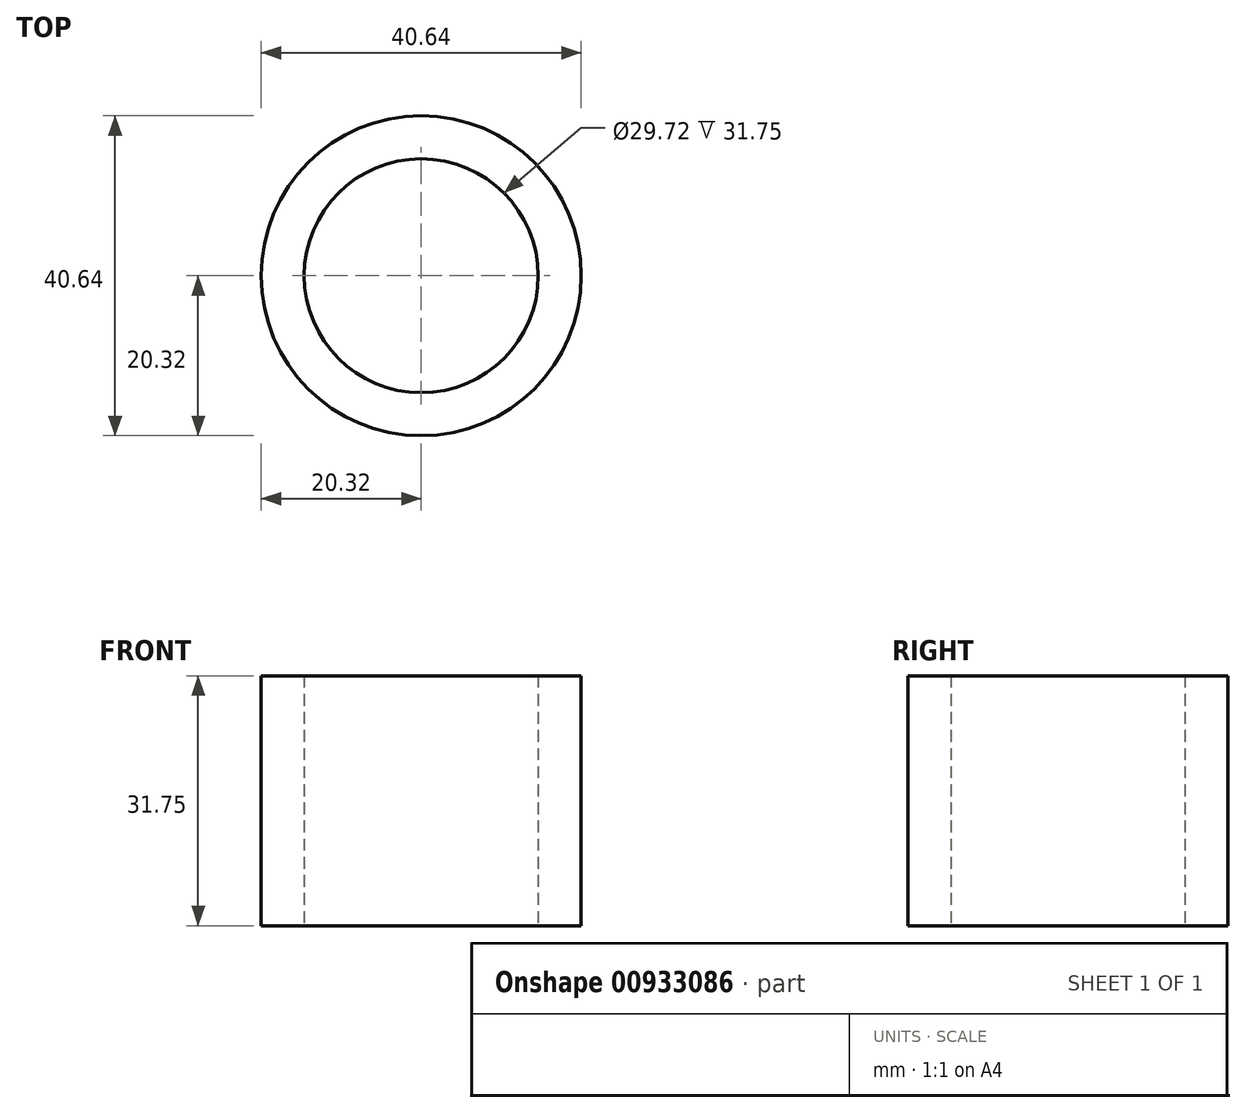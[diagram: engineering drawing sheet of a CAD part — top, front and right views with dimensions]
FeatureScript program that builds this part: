
annotation { "Feature Type Name" : "Feature", "Feature Type Description" : "" }
export const myFeature = defineFeature(function(context is Context, id is Id, definition is map)
    precondition{}
    {
        {
            var Q0;
            Q0=qCreatedBy(makeId("Top.planeOp"),FACE);
            var sketch = newSketch(context, id + "F0", { "sketchPlane" : qUnion([Q0])});
            skCircle(sketch, "E0", {"center": v(0, 0) * mm, "radius": 14.86 * mm});
            skCircle(sketch, "E1", {"center": v(0, 0) * mm, "radius": 20.32 * mm});
            skSolve(sketch);
        }
        {
            var Q0;
            Q0=makeQuery(id+"F0.imprint","IMPRINT",FACE,{"disambiguationData":[TD([[makeQuery(id+"F0.imprint","IMPRINT",EDGE,{"derivedFrom":sQuery(id+"F0.wireOp",EDGE,"E0")}),-1.0]])]});
            extrude(context, id + "F1", {"entities" : qUnion([Q0]), "depth" : 31.75 * mm, "offsetDistance" : 25.4 * mm});
        }
    });
